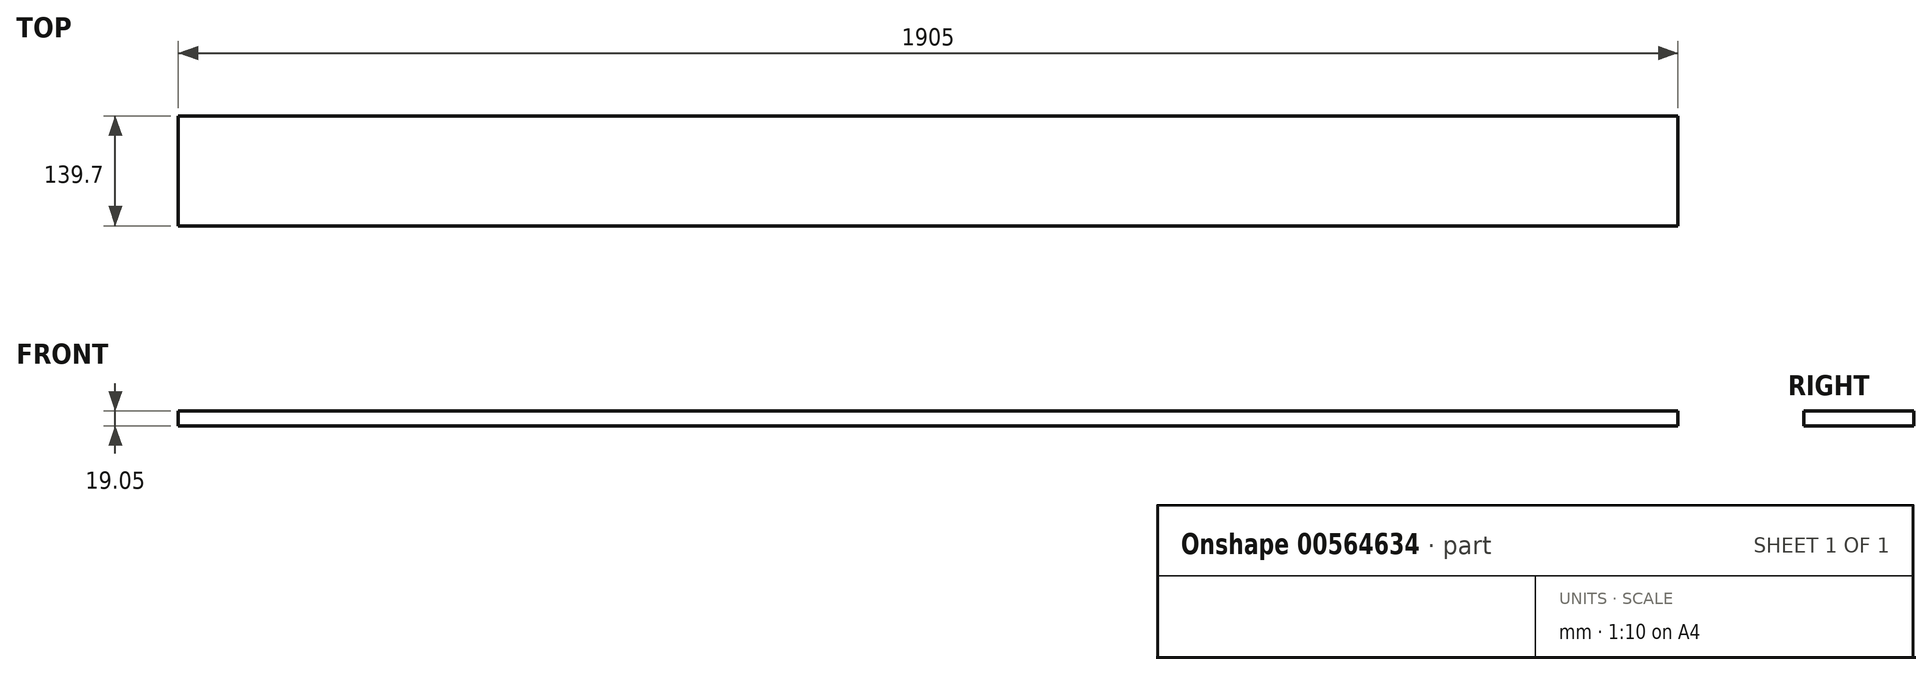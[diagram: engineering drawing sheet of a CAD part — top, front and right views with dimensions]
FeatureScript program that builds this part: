
annotation { "Feature Type Name" : "Feature", "Feature Type Description" : "" }
export const myFeature = defineFeature(function(context is Context, id is Id, definition is map)
    precondition{}
    {
        {
            var Q0;
            Q0=qCreatedBy(makeId("Top.planeOp"),FACE);
            var sketch = newSketch(context, id + "F0", { "sketchPlane" : qUnion([Q0])});
            skLineSegment(sketch, "E0.bottom", {"start": v(-952.5, 69.85) * mm, "end": v(952.5, 69.85) * mm});
            skLineSegment(sketch, "E0.top", {"start": v(-952.5, -69.85) * mm, "end": v(952.5, -69.85) * mm});
            skLineSegment(sketch, "E0.left", {"start": v(-952.5, 69.85) * mm, "end": v(-952.5, -69.85) * mm});
            skLineSegment(sketch, "E0.right", {"start": v(952.5, 69.85) * mm, "end": v(952.5, -69.85) * mm});
            skPoint(sketch, "E0.middle", {"position": v(0, 0) * mm});
            skSolve(sketch);
        }
        {
            var Q0;
            Q0=makeQuery(id+"F0.imprint","IMPRINT",FACE,{"disambiguationData":[TD([[makeQuery(id+"F0.imprint","IMPRINT",EDGE,{"derivedFrom":sQuery(id+"F0.wireOp",EDGE,"E0.bottom")}),-1.0]])]});
            extrude(context, id + "F1", {"entities" : qUnion([Q0]), "depth" : 19.05 * mm, "offsetDistance" : 25.4 * mm});
        }
    });
